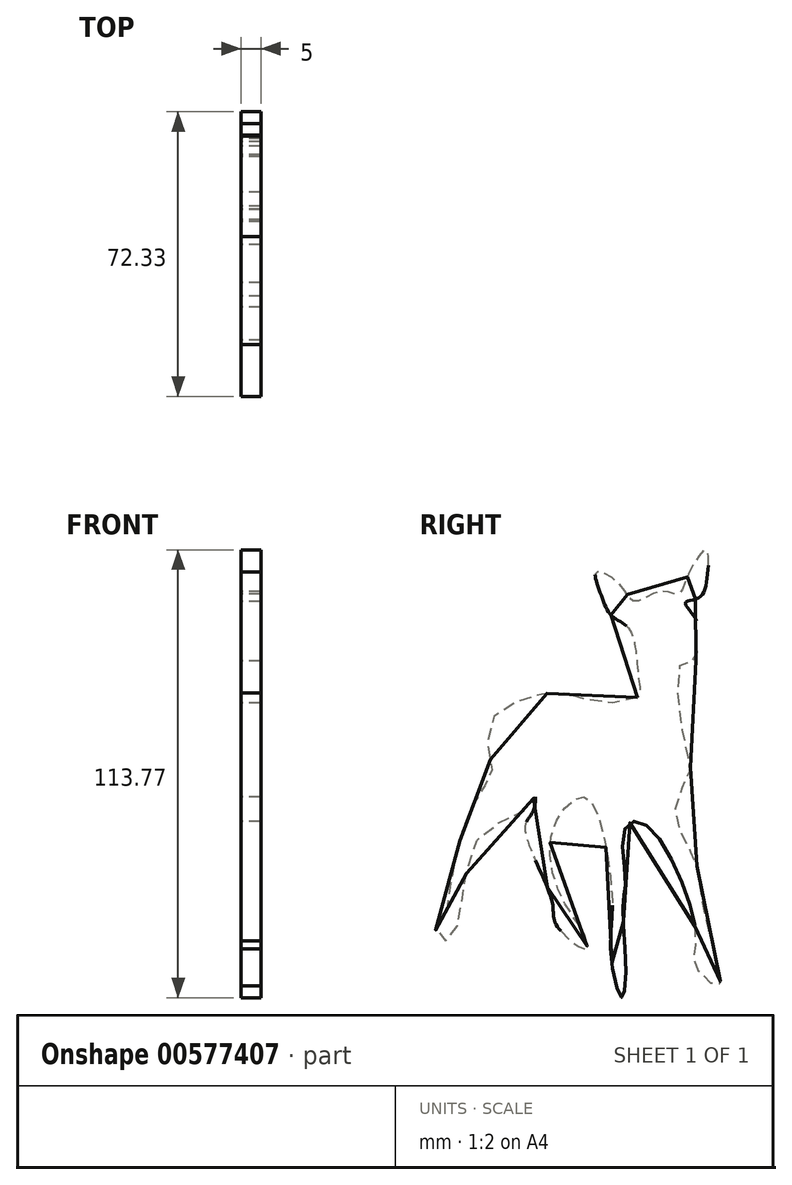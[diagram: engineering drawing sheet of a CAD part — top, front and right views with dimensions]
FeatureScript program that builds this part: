
annotation { "Feature Type Name" : "Feature", "Feature Type Description" : "" }
export const myFeature = defineFeature(function(context is Context, id is Id, definition is map)
    precondition{}
    {
        {
            var Q0;
            Q0=qCreatedBy(makeId("Right.planeOp"),FACE);
            var sketch = newSketch(context, id + "F0", { "sketchPlane" : qUnion([Q0])});
            skFitSpline(sketch, "E0", {"points": [v(6.48, 13.73) * mm, v(-2.92, 12.43) * mm, v(-10.37, 14.37) * mm, v(-16.52, 14.7) * mm, v(-25.27, 12.1) * mm, v(-31.43, 5.95) * mm, v(-30.46, -4.74) * mm, v(-31.75, -7.98) * mm, v(-35.96, -14.79) * mm, v(-38.88, -23.86) * mm, v(-40.82, -32.93) * mm, v(-42.44, -41.35) * mm, v(-44.71, -46.21) * mm, v(-41.47, -48.16) * mm, v(-38.56, -41.35) * mm, v(-36.94, -30.99) * mm, v(-32.08, -19.97) * mm, v(-22.68, -15.43) * mm, v(-19.44, -11.55) * mm, v(-20.09, -15.43) * mm, v(-22.03, -19.65) * mm, v(-15.23, -37.8) * mm, v(-14.58, -42.97) * mm, v(-10.04, -48.48) * mm, v(-6.48, -50.1) * mm, v(-7.13, -46.21) * mm, v(-11.66, -39.09) * mm, v(-15.55, -22.24) * mm, v(-8.75, -11.87) * mm, v(-4.54, -13.81) * mm, v(0, -35.52) * mm, v(0, -42.65) * mm, v(0, -53.34) * mm, v(2.6, -62.6) * mm, v(3.56, -53.67) * mm, v(2.92, -37.8) * mm, v(3.56, -33.9) * mm, v(3.24, -19.97) * mm, v(7.45, -18.03) * mm, v(17.5, -32.28) * mm, v(21.38, -48.16) * mm, v(20.74, -52.7) * mm, v(23, -56.9) * mm, v(27.22, -59.5) * mm, v(24.3, -43.95) * mm, v(22.36, -32.93) * mm, v(20.74, -26.77) * mm, v(16.2, -15.11) * mm, v(19.76, -5.4) * mm, v(19.12, 0) * mm, v(17.82, 22.47) * mm, v(21.38, 23.12) * mm, v(21.38, 28.95) * mm, v(21.38, 33.49) * mm, v(18.8, 37.7) * mm, v(22.03, 39) * mm, v(24.3, 44.5) * mm, v(23.98, 51.16) * mm, v(19.44, 44.83) * mm, v(16.85, 39.97) * mm, v(12.31, 40.62) * mm, v(5.83, 38.03) * mm, v(2.27, 42.24) * mm, v(-3.89, 45.48) * mm, v(-3.24, 41.27) * mm, v(0, 34.46) * mm, v(4.54, 30.9) * mm, v(6.8, 18.9) * mm, v(6.48, 13.73) * mm]});
            skSolve(sketch);
        }
        {
            var Q0;
            Q0 = qSketchRegion(id + "F0", true);
            extrude(context, id + "F1", {"entities" : qUnion([Q0]), "depth" : 5 * mm, "offsetDistance" : 25 * mm});
        }
    });
